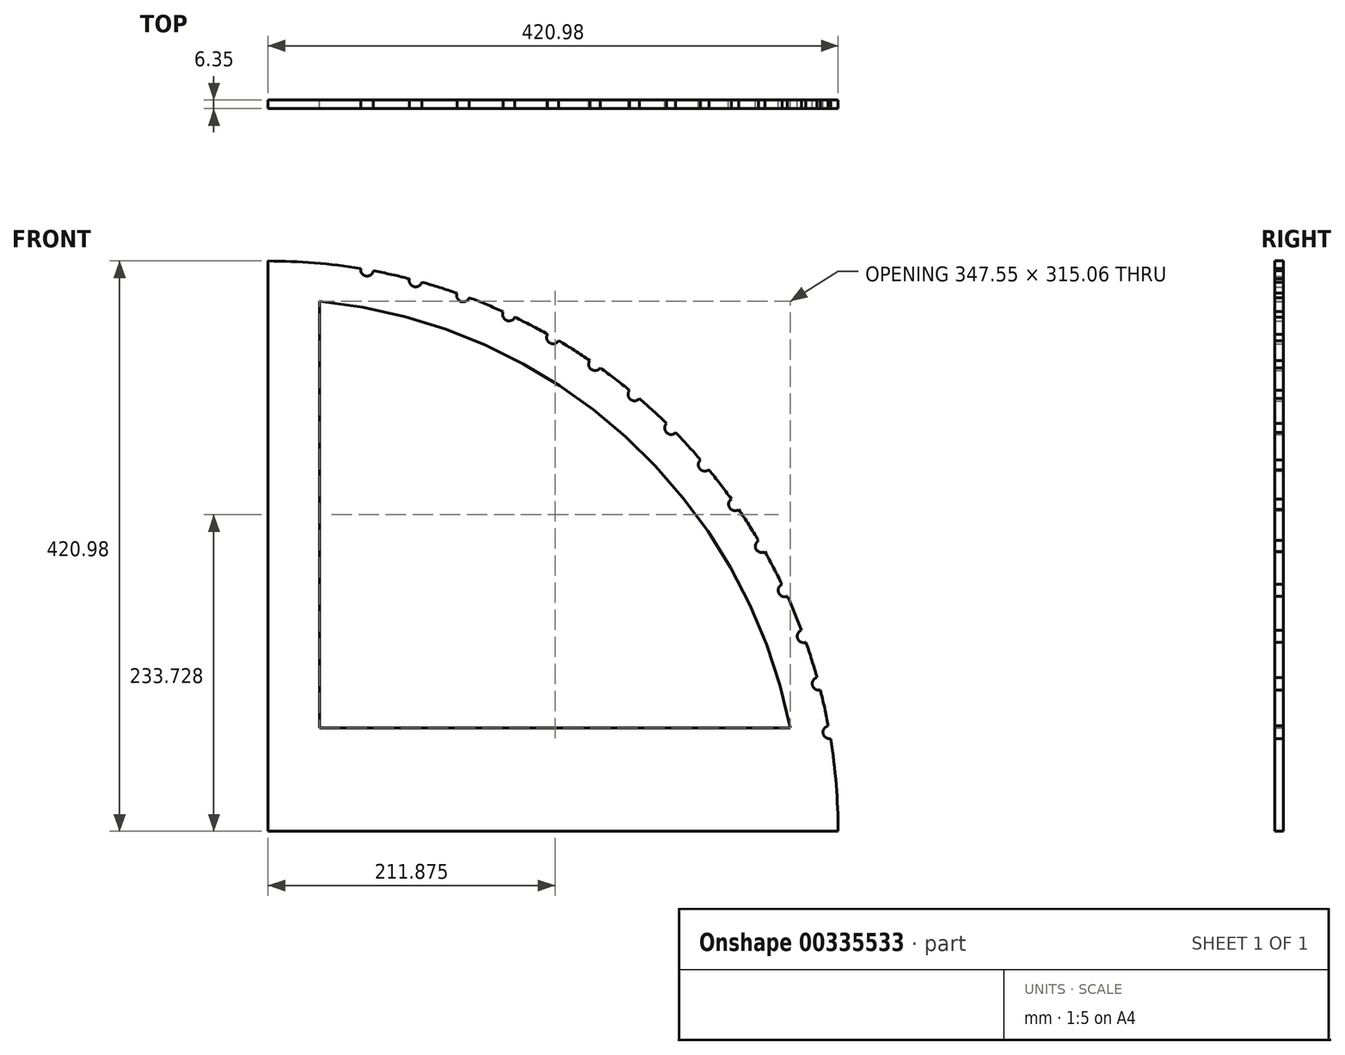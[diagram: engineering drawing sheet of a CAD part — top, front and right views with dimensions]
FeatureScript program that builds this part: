
annotation { "Feature Type Name" : "Feature", "Feature Type Description" : "" }
export const myFeature = defineFeature(function(context is Context, id is Id, definition is map)
    precondition{}
    {
        {
            var Q0;
            Q0=qCreatedBy(makeId("Front.planeOp"),FACE);
            var sketch = newSketch(context, id + "F0", { "sketchPlane" : qUnion([Q0])});
            skLineSegment(sketch, "E0", {"start": v(0, 0) * mm, "end": v(0, 457.2) * mm});
            skLineSegment(sketch, "E1", {"start": v(0, 0) * mm, "end": v(457.2, 0) * mm});
            skArc(sketch, "E2", {"start": v(0, 457.2) * mm, "mid": v(323.29, 323.29) * mm, "end": v(457.2, 0) * mm});
            skArc(sketch, "E3", {"start": v(0, 420.98) * mm, "mid": v(297.68, 297.68) * mm, "end": v(420.98, 0) * mm});
            skCircle(sketch, "E4", {"center": v(414.58, 73.1) * mm, "radius": 4.76 * mm});
            skCircle(sketch, "E5", {"center": v(406.64, 108.96) * mm, "radius": 4.76 * mm});
            skCircle(sketch, "E6", {"center": v(395.6, 143.98) * mm, "radius": 4.76 * mm});
            skCircle(sketch, "E7", {"center": v(381.54, 177.91) * mm, "radius": 4.76 * mm});
            skCircle(sketch, "E8", {"center": v(364.58, 210.49) * mm, "radius": 4.76 * mm});
            skCircle(sketch, "E9", {"center": v(344.85, 241.46) * mm, "radius": 4.76 * mm});
            skCircle(sketch, "E10", {"center": v(322.49, 270.6) * mm, "radius": 4.76 * mm});
            skCircle(sketch, "E11", {"center": v(297.68, 297.68) * mm, "radius": 4.76 * mm});
            skCircle(sketch, "E12", {"center": v(270.6, 322.49) * mm, "radius": 4.76 * mm});
            skCircle(sketch, "E13", {"center": v(241.46, 344.85) * mm, "radius": 4.76 * mm});
            skCircle(sketch, "E14", {"center": v(210.49, 364.58) * mm, "radius": 4.76 * mm});
            skCircle(sketch, "E15", {"center": v(177.91, 381.54) * mm, "radius": 4.76 * mm});
            skCircle(sketch, "E16", {"center": v(143.98, 395.6) * mm, "radius": 4.76 * mm});
            skCircle(sketch, "E17", {"center": v(108.96, 406.64) * mm, "radius": 4.76 * mm});
            skCircle(sketch, "E18", {"center": v(73.1, 414.58) * mm, "radius": 4.76 * mm});
            skLineSegment(sketch, "E19", {"start": v(38.1, 76.2) * mm, "end": v(38.1, 391.26) * mm});
            skArc(sketch, "E20", {"start": v(38.1, 391.26) * mm, "mid": v(264.02, 291.25) * mm, "end": v(385.65, 76.2) * mm});
            skLineSegment(sketch, "E21", {"start": v(38.1, 76.2) * mm, "end": v(385.65, 76.2) * mm});
            skSolve(sketch);
        }
        {
            var Q0;
            {var subQ1=sQuery(id+"F0.wireOp",EDGE,"E1");var subQ39=sQuery(id+"F0.wireOp",EDGE,"E0");var subQ40=makeQuery(id+"F0.imprint","INTERSECT",VERTEX,{"derivedFrom":[subQ39,subQ1]});Q0=makeQuery(id+"F0.imprint","IMPRINT",FACE,{"disambiguationData":[TD([[makeQuery(id+"F0.imprint","IMPRINT",EDGE,{"disambiguationData":[TD([[subQ40,-1.0]])],"derivedFrom":subQ39}),-1.0]])]});}
            var Q1;
            {var subQ39=sQuery(id+"F0.wireOp",EDGE,"E2");Q1=makeQuery(id+"F0.imprint","IMPRINT",FACE,{"disambiguationData":[TD([[makeQuery(id+"F0.imprint","IMPRINT",EDGE,{"derivedFrom":subQ39}),-1.0]])]});}
            extrude(context, id + "F1", {"entities" : qUnion([Q0, Q1]), "depth" : 6.35 * mm});
        }
    });
